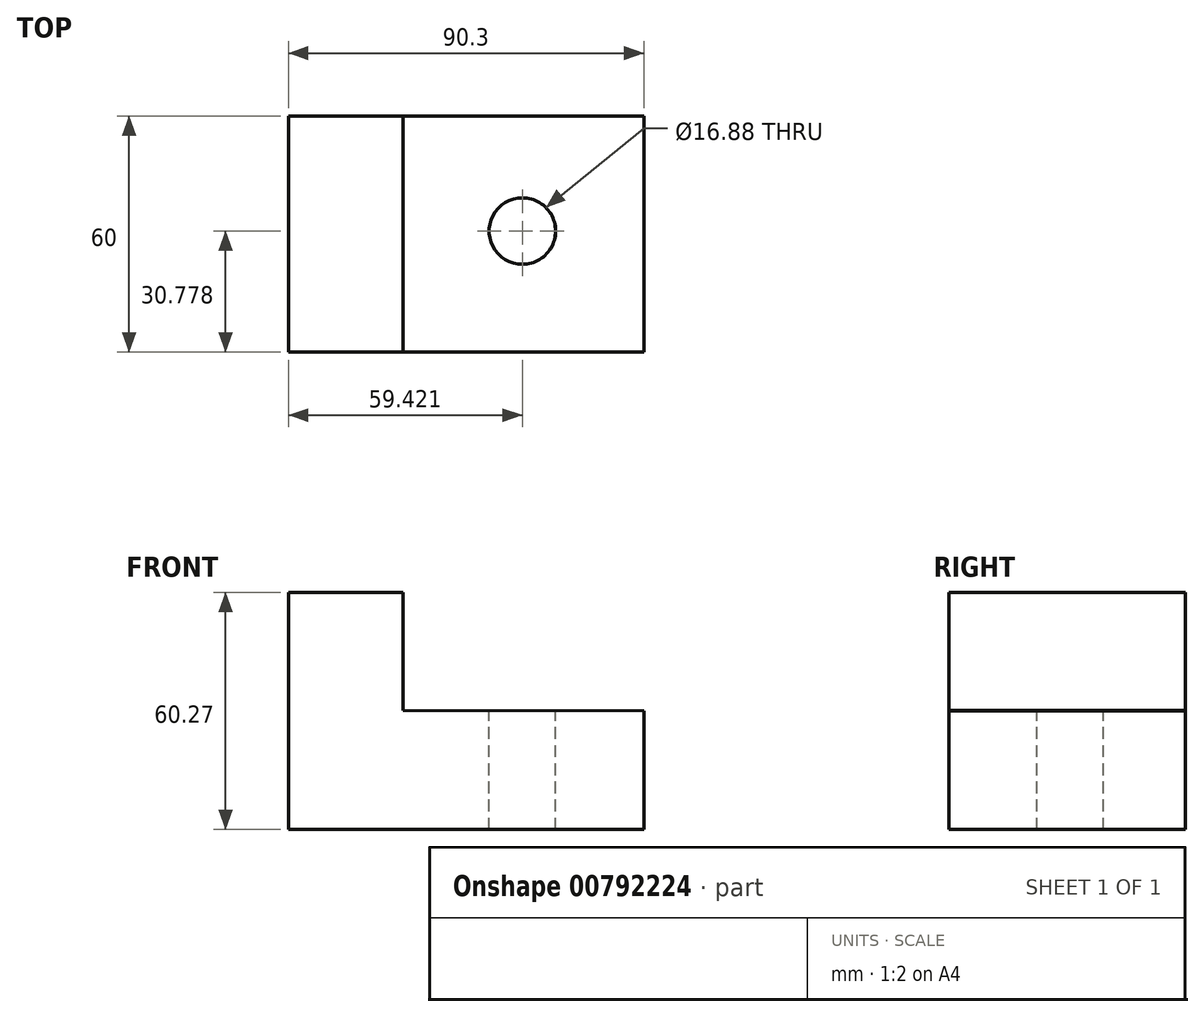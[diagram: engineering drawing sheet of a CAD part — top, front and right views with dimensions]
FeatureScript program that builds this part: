
annotation { "Feature Type Name" : "Feature", "Feature Type Description" : "" }
export const myFeature = defineFeature(function(context is Context, id is Id, definition is map)
    precondition{}
    {
        {
            var Q0;
            Q0=qCreatedBy(makeId("Front.planeOp"),FACE);
            var sketch = newSketch(context, id + "F0", { "sketchPlane" : qUnion([Q0])});
            skLineSegment(sketch, "E0", {"start": v(-38.78, 16.49) * mm, "end": v(-38.78, -13.78) * mm});
            skLineSegment(sketch, "E1", {"start": v(-38.78, -13.78) * mm, "end": v(51.52, -13.78) * mm});
            skLineSegment(sketch, "E2", {"start": v(51.52, -13.78) * mm, "end": v(51.52, 16.4) * mm});
            skLineSegment(sketch, "E3", {"start": v(51.52, 16.4) * mm, "end": v(-38.78, 16.49) * mm});
            skSolve(sketch);
        }
        {
            var Q0;
            Q0=makeQuery(id+"F0.imprint","IMPRINT",FACE,{"disambiguationData":[TD([[makeQuery(id+"F0.imprint","IMPRINT",EDGE,{"derivedFrom":sQuery(id+"F0.wireOp",EDGE,"E0")}),1.0]])]});
            extrude(context, id + "F1", {"entities" : qUnion([Q0]), "oppositeDirection" : true, "depth" : 60 * mm, "offsetDistance" : 25 * mm});
        }
        {
            var Q0;
            Q0=makeQuery(id+"F1.opExtrude","SWEPT_FACE",FACE,{"disambiguationData":[OSD([sQuery(id+"F0.wireOp",EDGE,"E3")])]});
            var sketch = newSketch(context, id + "F2", { "sketchPlane" : qUnion([Q0])});
            skLineSegment(sketch, "E4", {"start": v(-38.8, 60) * mm, "end": v(-9.75, 60) * mm});
            skLineSegment(sketch, "E5", {"start": v(-9.75, 60) * mm, "end": v(-9.75, 0) * mm});
            skLineSegment(sketch, "E6", {"start": v(-9.75, 0) * mm, "end": v(-38.8, 0) * mm});
            skLineSegment(sketch, "E7", {"start": v(-38.8, 0) * mm, "end": v(-38.8, 60) * mm});
            skSolve(sketch);
        }
        {
            var Q0;
            Q0=makeQuery(id+"F2.imprint","IMPRINT",FACE,{"disambiguationData":[TD([[makeQuery(id+"F2.imprint","IMPRINT",EDGE,{"derivedFrom":sQuery(id+"F2.wireOp",EDGE,"E4")}),1.0]])]});
            extrude(context, id + "F3", {"entities" : qUnion([Q0]), "operationType" : NewBodyOperationType.ADD, "depth" : 30 * mm, "offsetDistance" : 25 * mm});
        }
        {
            var Q0;
            Q0=makeQuery(id+"F1.opExtrude","SWEPT_FACE",FACE,{"disambiguationData":[OSD([sQuery(id+"F0.wireOp",EDGE,"E3")])]});
            var sketch = newSketch(context, id + "F4", { "sketchPlane" : qUnion([Q0])});
            skCircle(sketch, "E8", {"center": v(20.64, 30.78) * mm, "radius": 8.44 * mm});
            skSolve(sketch);
        }
        {
            var Q0;
            Q0=makeQuery(id+"F4.imprint","IMPRINT",FACE,{"disambiguationData":[TD([[makeQuery(id+"F4.imprint","IMPRINT",EDGE,{"derivedFrom":sQuery(id+"F4.wireOp",EDGE,"E8")}),1.0]])]});
            extrude(context, id + "F5", {"entities" : qUnion([Q0]), "operationType" : NewBodyOperationType.REMOVE, "oppositeDirection" : true, "depth" : 49 * mm, "offsetDistance" : 25 * mm});
        }
    });
